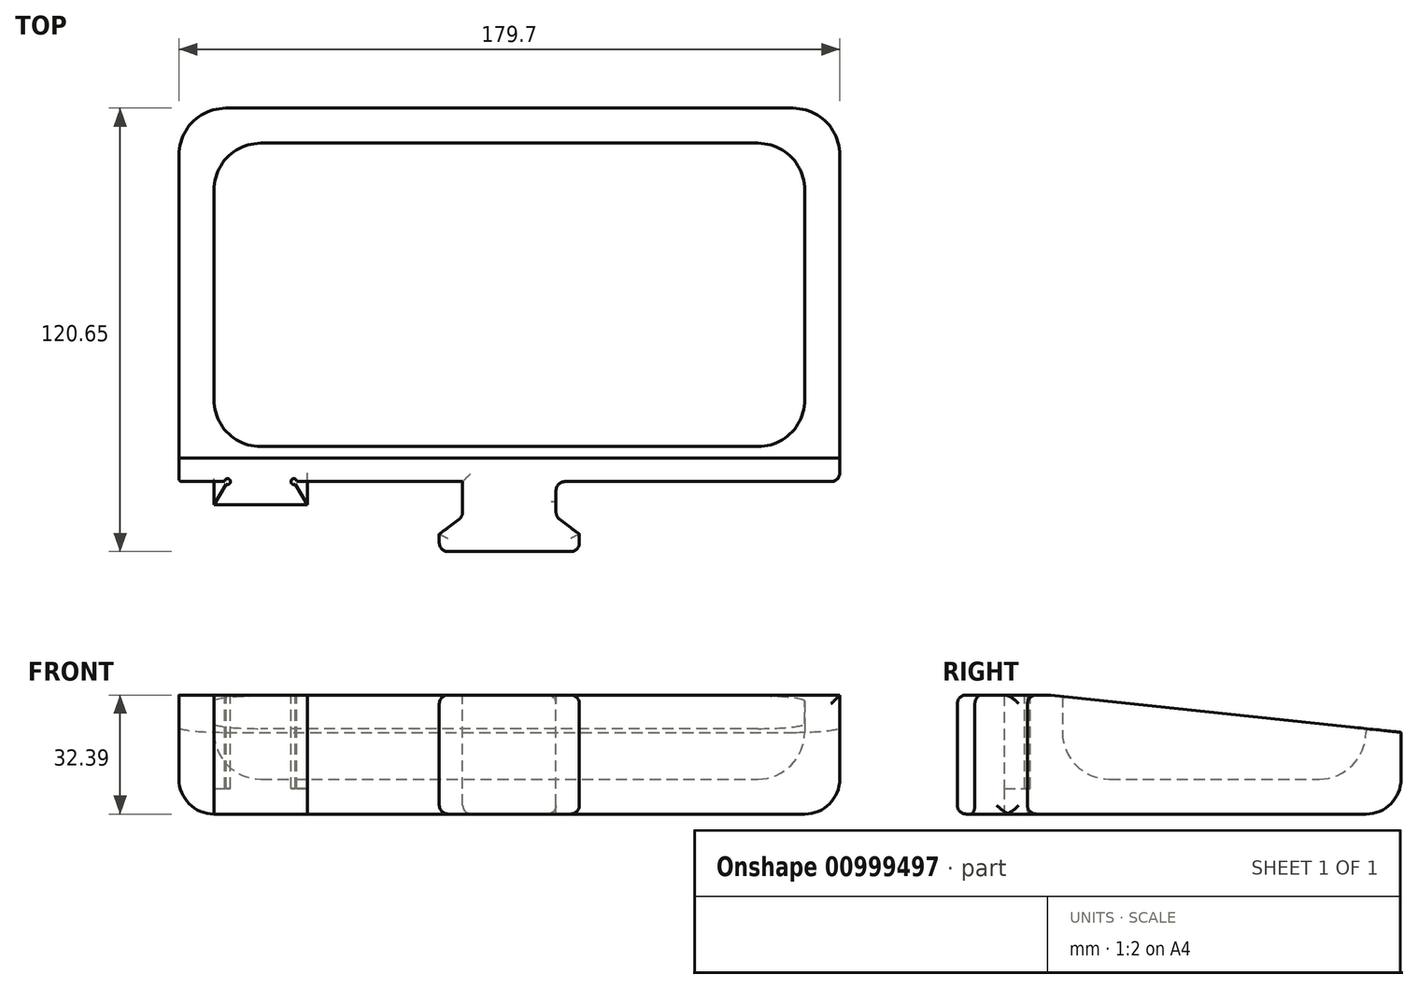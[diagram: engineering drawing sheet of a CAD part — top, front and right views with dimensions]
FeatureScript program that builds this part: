
annotation { "Feature Type Name" : "Feature", "Feature Type Description" : "" }
export const myFeature = defineFeature(function(context is Context, id is Id, definition is map)
    precondition{}
    {
        {
            var Q0;
            Q0=qCreatedBy(makeId("Top.planeOp"),FACE);
            var sketch = newSketch(context, id + "F0", { "sketchPlane" : qUnion([Q0])});
            skLineSegment(sketch, "E0.bottom", {"start": v(-89.85, -50.8) * mm, "end": v(89.85, -50.8) * mm});
            skLineSegment(sketch, "E0.top", {"start": v(-89.85, 50.8) * mm, "end": v(89.85, 50.8) * mm});
            skLineSegment(sketch, "E0.left", {"start": v(-89.85, -50.8) * mm, "end": v(-89.85, 50.8) * mm});
            skLineSegment(sketch, "E0.right", {"start": v(89.85, -50.8) * mm, "end": v(89.85, 50.8) * mm});
            skPoint(sketch, "E0.middle", {"position": v(0, 0) * mm});
            skSolve(sketch);
        }
        {
            var Q0;
            Q0=makeQuery(id+"F0.imprint","IMPRINT",FACE,{"disambiguationData":[TD([[makeQuery(id+"F0.imprint","IMPRINT",EDGE,{"derivedFrom":sQuery(id+"F0.wireOp",EDGE,"E0.bottom")}),1.0]])]});
            extrude(context, id + "F1", {"entities" : qUnion([Q0]), "depth" : 32.38 * mm, "offsetDistance" : 25.4 * mm});
        }
        {
            var Q0;
            Q0=makeQuery(id+"F1.opExtrude","SWEPT_FACE",FACE,{"disambiguationData":[OSD([sQuery(id+"F0.wireOp",EDGE,"E0.right")])]});
            var sketch = newSketch(context, id + "F2", { "sketchPlane" : qUnion([Q0])});
            skLineSegment(sketch, "E1", {"start": v(-44.45, 32.39) * mm, "end": v(50.8, 22.23) * mm});
            skLineSegment(sketch, "E2", {"start": v(50.8, 22.23) * mm, "end": v(50.8, 32.39) * mm});
            skLineSegment(sketch, "E3", {"start": v(50.8, 32.39) * mm, "end": v(-44.45, 32.39) * mm});
            skSolve(sketch);
        }
        {
            var Q0;
            Q0=makeQuery(id+"F4zIDM2y6RTGsAz_1.boolean.opBoolean","MERGE",FACE,{"derivedFrom":[makeQuery(id+"F1.opExtrude","CAP_FACE",FACE,{"disambiguationData":[OSD([sQuery(id+"F0.wireOp",EDGE,"E0.bottom"),sQuery(id+"F0.wireOp",EDGE,"E0.top"),sQuery(id+"F0.wireOp",EDGE,"E0.left"),sQuery(id+"F0.wireOp",EDGE,"E0.right")])],"isStart":false})],"fromTools":[makeQuery(id+"F4zIDM2y6RTGsAz_1.opExtrude","SWEPT_FACE",FACE,{"disambiguationData":[OSD([sQuery(id+"FbF38NB3fGvbLQ3_1.wireOp",EDGE,"ddc0e0ec-bf3b-4cb0-ae8b-31f4564a783b.bottom")])]})]});
            shell(context, id + "F3", {"entities" : qUnion([Q0]), "thickness" : 9.52 * mm});
        }
        {
            var Q0;
            Q0=makeQuery(id+"F2.imprint","IMPRINT",FACE,{"disambiguationData":[TD([[makeQuery(id+"F2.imprint","IMPRINT",EDGE,{"derivedFrom":sQuery(id+"F2.wireOp",EDGE,"E1")}),1.0]])]});
            extrude(context, id + "F4", {"entities" : qUnion([Q0]), "operationType" : NewBodyOperationType.REMOVE, "endBound" : BoundingType.THROUGH_ALL, "oppositeDirection" : true, "depth" : 25.4 * mm, "offsetDistance" : 25.4 * mm});
        }
        {
            var Q0;
            Q0=makeQuery(id+"Ffoehrqari5NT87_1.boolean.opBoolean","MERGE",FACE,{"derivedFrom":[makeQuery(id+"F1.opExtrude","SWEPT_FACE",FACE,{"disambiguationData":[OSD([sQuery(id+"F0.wireOp",EDGE,"E0.bottom")])]}),makeQuery(id+"Ffoehrqari5NT87_1.opExtrude","SWEPT_FACE",FACE,{"disambiguationData":[OSD([sQuery(id+"F7CfLhOei2jAQx5_1.wireOp",EDGE,"9709d949-b5b5-4919-9016-7ddb15cc25a9.left")])]})]});
            var sketch = newSketch(context, id + "F5", { "sketchPlane" : qUnion([Q0])});
            skLineSegment(sketch, "E4", {"start": v(0, 0) * mm, "end": v(0, 32.39) * mm, "construction": true});
            skLineSegment(sketch, "E5", {"start": v(-19.05, 0) * mm, "end": v(-19.05, 32.39) * mm});
            skLineSegment(sketch, "E6.MirrorCS", {"start": v(19.05, 0) * mm, "end": v(19.05, 32.39) * mm});
            skLineSegment(sketch, "E7", {"start": v(-19.05, 32.39) * mm, "end": v(19.05, 32.39) * mm});
            skLineSegment(sketch, "E8", {"start": v(-19.05, 0) * mm, "end": v(19.05, 0) * mm});
            skSolve(sketch);
        }
        {
            var Q0;
            Q0=makeQuery(id+"F5.imprint","IMPRINT",FACE,{"disambiguationData":[TD([[makeQuery(id+"F5.imprint","IMPRINT",EDGE,{"derivedFrom":sQuery(id+"F5.wireOp",EDGE,"E5")}),-1.0]])]});
            extrude(context, id + "F6", {"entities" : qUnion([Q0]), "operationType" : NewBodyOperationType.ADD, "depth" : 19.05 * mm, "offsetDistance" : 25.4 * mm});
        }
        {
            var Q0;
            {var subQ0=sQuery(id+"F0.wireOp",EDGE,"E0.left");var subQ1=makeQuery(id+"F1.opExtrude","SWEPT_FACE",FACE,{"disambiguationData":[OSD([subQ0])]});var subQ4=sQuery(id+"F0.wireOp",EDGE,"E0.bottom");Q0=makeQuery(id+"F6.boolean.opBoolean","SPLIT",FACE,{"disambiguationData":[TD([subQ1])],"derivedFrom":makeQuery(id+"F1.opExtrude","SWEPT_FACE",FACE,{"disambiguationData":[OSD([subQ4])]})});}
            var sketch = newSketch(context, id + "F7", { "sketchPlane" : qUnion([Q0])});
            skLineSegment(sketch, "E9.bottom", {"start": v(-80.33, 32.38) * mm, "end": v(-54.93, 32.39) * mm});
            skLineSegment(sketch, "E9.top", {"start": v(-80.33, 0) * mm, "end": v(-54.93, 0) * mm});
            skLineSegment(sketch, "E9.left", {"start": v(-80.33, 32.39) * mm, "end": v(-80.33, 0) * mm});
            skLineSegment(sketch, "E9.right", {"start": v(-54.93, 32.38) * mm, "end": v(-54.93, 0) * mm});
            skSolve(sketch);
        }
        {
            var Q0;
            Q0=makeQuery(id+"F7.imprint","IMPRINT",FACE,{"disambiguationData":[TD([[makeQuery(id+"F7.imprint","IMPRINT",EDGE,{"derivedFrom":sQuery(id+"F7.wireOp",EDGE,"E9.bottom")}),-1.0]])]});
            extrude(context, id + "F8", {"entities" : qUnion([Q0]), "operationType" : NewBodyOperationType.ADD, "depth" : 6.35 * mm, "offsetDistance" : 25.4 * mm});
        }
        {
            var Q0;
            Q0=makeQuery(id+"F8.boolean.opBoolean","MERGE",FACE,{"derivedFrom":[makeQuery(id+"F6.boolean.opBoolean","MERGE",FACE,{"derivedFrom":[makeQuery(id+"F1.opExtrude","CAP_FACE",FACE,{"disambiguationData":[OSD([sQuery(id+"F0.wireOp",EDGE,"E0.bottom"),sQuery(id+"F0.wireOp",EDGE,"E0.top"),sQuery(id+"F0.wireOp",EDGE,"E0.left"),sQuery(id+"F0.wireOp",EDGE,"E0.right")])],"isStart":false}),makeQuery(id+"F6.opExtrude","SWEPT_FACE",FACE,{"disambiguationData":[OSD([sQuery(id+"F5.wireOp",EDGE,"E7")])]})]}),makeQuery(id+"F8.opExtrude","SWEPT_FACE",FACE,{"disambiguationData":[OSD([sQuery(id+"F7.wireOp",EDGE,"E9.bottom")])]})]});
            var sketch = newSketch(context, id + "F9", { "sketchPlane" : qUnion([Q0])});
            skLineSegment(sketch, "E10", {"start": v(-80.33, -50.8) * mm, "end": v(-54.93, -50.8) * mm});
            skLineSegment(sketch, "E11", {"start": v(-80.33, -57.15) * mm, "end": v(-76.66, -50.8) * mm});
            skLineSegment(sketch, "E12", {"start": v(-67.63, -57.15) * mm, "end": v(-67.63, -50.8) * mm, "construction": true});
            skLineSegment(sketch, "E13.MirrorCS", {"start": v(-54.93, -57.15) * mm, "end": v(-58.6, -50.8) * mm});
            skCircle(sketch, "E14", {"center": v(-76.66, -50.8) * mm, "radius": 0.8 * mm});
            skCircle(sketch, "E15.MirrorC", {"center": v(-58.6, -50.8) * mm, "radius": 0.8 * mm});
            skSolve(sketch);
        }
        {
            var Q0;
            {var subQ11=sQuery(id+"F9.wireOp",EDGE,"E11");Q0=makeQuery(id+"F9.imprint","IMPRINT",FACE,{"disambiguationData":[TD([[makeQuery(id+"F9.imprint","IMPRINT",EDGE,{"derivedFrom":subQ11}),1.0]])]});}
            var Q1;
            {var subQ11=sQuery(id+"F9.wireOp",EDGE,"E13.MirrorCS");Q1=makeQuery(id+"F9.imprint","IMPRINT",FACE,{"disambiguationData":[TD([[makeQuery(id+"F9.imprint","IMPRINT",EDGE,{"derivedFrom":subQ11}),-1.0]])]});}
            var Q2;
            {var subQ3=sQuery(id+"F7.wireOp",EDGE,"E9.bottom");var subQ5=sQuery(id+"F0.wireOp",EDGE,"E0.bottom");var subQ8=sQuery(id+"F7.wireOp",EDGE,"E9.left");var subQ9=makeQuery(id+"F8.opExtrude","SWEPT_EDGE",EDGE,{"disambiguationData":[OSD([subQ5,subQ3,subQ8])]});Q2=makeQuery(id+"F9.imprint","IMPRINT",FACE,{"disambiguationData":[TD([[makeQuery(id+"F9.imprint","IMPRINT",EDGE,{"derivedFrom":subQ9}),-1.0]])]});}
            var Q3;
            {var subQ0=sQuery(id+"F9.wireOp",EDGE,"E14");var subQ1=sQuery(id+"F9.wireOp",EDGE,"E10");var subQ2=makeQuery(id+"F9.imprint","INTERSECT",VERTEX,{"disambiguationData":[OD(0.0)],"derivedFrom":[subQ1,subQ0]});Q3=makeQuery(id+"F9.imprint","IMPRINT",FACE,{"disambiguationData":[TD([[makeQuery(id+"F9.imprint","IMPRINT",EDGE,{"disambiguationData":[TD([[subQ2,1.0]])],"derivedFrom":subQ1}),-1.0]])]});}
            var Q4;
            {var subQ0=sQuery(id+"F9.wireOp",EDGE,"E14");var subQ1=sQuery(id+"F9.wireOp",EDGE,"E10");var subQ2=makeQuery(id+"F9.imprint","INTERSECT",VERTEX,{"disambiguationData":[OD(0.0)],"derivedFrom":[subQ1,subQ0]});Q4=makeQuery(id+"F9.imprint","IMPRINT",FACE,{"disambiguationData":[TD([[makeQuery(id+"F9.imprint","IMPRINT",EDGE,{"disambiguationData":[TD([[subQ2,1.0]])],"derivedFrom":subQ1}),1.0]])]});}
            var Q5;
            {var subQ4=sQuery(id+"F0.wireOp",EDGE,"E0.bottom");var subQ7=sQuery(id+"F7.wireOp",EDGE,"E9.bottom");var subQ8=sQuery(id+"F7.wireOp",EDGE,"E9.right");var subQ9=makeQuery(id+"F8.opExtrude","SWEPT_EDGE",EDGE,{"disambiguationData":[OSD([subQ4,subQ7,subQ8])]});Q5=makeQuery(id+"F9.imprint","IMPRINT",FACE,{"disambiguationData":[TD([[makeQuery(id+"F9.imprint","IMPRINT",EDGE,{"derivedFrom":subQ9}),1.0]])]});}
            var Q6;
            {var subQ0=sQuery(id+"F9.wireOp",EDGE,"E10");var subQ1=makeQuery(id+"F9.imprint","INTERSECT",VERTEX,{"derivedFrom":[subQ0,sQuery(id+"F9.wireOp",EDGE,"E13.MirrorCS")]});Q6=makeQuery(id+"F9.imprint","IMPRINT",FACE,{"disambiguationData":[TD([[makeQuery(id+"F9.imprint","IMPRINT",EDGE,{"disambiguationData":[TD([[subQ1,-1.0]])],"derivedFrom":subQ0}),1.0]])]});}
            var Q7;
            {var subQ0=sQuery(id+"F9.wireOp",EDGE,"E13.MirrorCS");var subQ1=sQuery(id+"F9.wireOp",EDGE,"E10");var subQ2=makeQuery(id+"F9.imprint","INTERSECT",VERTEX,{"derivedFrom":[subQ1,subQ0]});Q7=makeQuery(id+"F9.imprint","IMPRINT",FACE,{"disambiguationData":[TD([[makeQuery(id+"F9.imprint","IMPRINT",EDGE,{"disambiguationData":[TD([[subQ2,1.0]])],"derivedFrom":subQ1}),-1.0]])]});}
            extrude(context, id + "F10", {"entities" : qUnion([Q0, Q1, Q2, Q3, Q4, Q5, Q6, Q7]), "operationType" : NewBodyOperationType.REMOVE, "oppositeDirection" : true, "depth" : 25.4 * mm, "offsetDistance" : 25.4 * mm});
        }
        {
            var Q0;
            Q0=makeQuery(id+"F3.opShell","OFFSET_EDGE",EDGE,{"disambiguationData":[OSD([sQuery(id+"F0.wireOp",EDGE,"E0.bottom"),sQuery(id+"F0.wireOp",EDGE,"E0.left")])]});
            var Q1;
            Q1=makeQuery(id+"F3.opShell","OFFSET_EDGE",EDGE,{"disambiguationData":[OSD([sQuery(id+"F0.wireOp",EDGE,"E0.bottom"),sQuery(id+"F0.wireOp",EDGE,"E0.right")])]});
            var Q2;
            Q2=makeQuery(id+"F3.opShell","OFFSET_EDGE",EDGE,{"disambiguationData":[OSD([sQuery(id+"F0.wireOp",EDGE,"E0.top"),sQuery(id+"F0.wireOp",EDGE,"E0.right")])]});
            var Q3;
            Q3=makeQuery(id+"F3.opShell","OFFSET_EDGE",EDGE,{"disambiguationData":[OSD([sQuery(id+"F0.wireOp",EDGE,"E0.top"),sQuery(id+"F0.wireOp",EDGE,"E0.left")])]});
            var Q4;
            {var subQ0=sQuery(id+"F0.wireOp",EDGE,"E0.left");Q4=makeQuery(id+"F3.opShell","OFFSET_EDGE",EDGE,{"disambiguationData":[OSD([subQ0]),TDD([makeQuery(id+"F1.opExtrude","CAP_EDGE",EDGE,{"disambiguationData":[OSD([subQ0])],"isStart":true})])]});}
            var Q5;
            {var subQ0=sQuery(id+"F0.wireOp",EDGE,"E0.top");Q5=makeQuery(id+"F3.opShell","OFFSET_EDGE",EDGE,{"disambiguationData":[OSD([subQ0]),TDD([makeQuery(id+"F1.opExtrude","CAP_EDGE",EDGE,{"disambiguationData":[OSD([subQ0])],"isStart":true})])]});}
            var Q6;
            {var subQ0=sQuery(id+"F0.wireOp",EDGE,"E0.right");Q6=makeQuery(id+"F3.opShell","OFFSET_EDGE",EDGE,{"disambiguationData":[OSD([subQ0]),TDD([makeQuery(id+"F1.opExtrude","CAP_EDGE",EDGE,{"disambiguationData":[OSD([subQ0])],"isStart":true})])]});}
            var Q7;
            {var subQ0=sQuery(id+"F0.wireOp",EDGE,"E0.bottom");Q7=makeQuery(id+"F3.opShell","OFFSET_EDGE",EDGE,{"disambiguationData":[OSD([subQ0]),TDD([makeQuery(id+"F1.opExtrude","CAP_EDGE",EDGE,{"disambiguationData":[OSD([subQ0])],"isStart":true})])]});}
            fillet(context, id + "F11", {"entities" : qUnion([Q0, Q1, Q2, Q3, Q4, Q5, Q6, Q7]), "tangentPropagation" : true, "radius" : 12.7 * mm, "defaultsChanged" : false, "vertexSettings" : [], "allowEdgeOverflow" : false});
        }
        {
            var Q0;
            Q0=makeQuery(id+"F8.boolean.opBoolean","MERGE",FACE,{"derivedFrom":[makeQuery(id+"F6.boolean.opBoolean","MERGE",FACE,{"derivedFrom":[makeQuery(id+"F1.opExtrude","CAP_FACE",FACE,{"disambiguationData":[OSD([sQuery(id+"F0.wireOp",EDGE,"E0.bottom"),sQuery(id+"F0.wireOp",EDGE,"E0.top"),sQuery(id+"F0.wireOp",EDGE,"E0.left"),sQuery(id+"F0.wireOp",EDGE,"E0.right")])],"isStart":false}),makeQuery(id+"F6.opExtrude","SWEPT_FACE",FACE,{"disambiguationData":[OSD([sQuery(id+"F5.wireOp",EDGE,"E7")])]})]}),makeQuery(id+"F8.opExtrude","SWEPT_FACE",FACE,{"disambiguationData":[OSD([sQuery(id+"F7.wireOp",EDGE,"E9.bottom")])]})]});
            var sketch = newSketch(context, id + "F12", { "sketchPlane" : qUnion([Q0])});
            skLineSegment(sketch, "E16", {"start": v(-19.05, -65.09) * mm, "end": v(-12.7, -60.33) * mm});
            skPoint(sketch, "E16.endSnap0", {"position": v(-19.05, -60.33) * mm});
            skLineSegment(sketch, "E17", {"start": v(-12.7, -60.33) * mm, "end": v(-12.7, -50.8) * mm});
            skLineSegment(sketch, "E18", {"start": v(-12.7, -50.8) * mm, "end": v(-19.05, -50.8) * mm});
            skLineSegment(sketch, "E19", {"start": v(-19.05, -50.8) * mm, "end": v(-19.05, -65.09) * mm});
            skLineSegment(sketch, "E20", {"start": v(0, -69.85) * mm, "end": v(0, -50.8) * mm, "construction": true});
            skLineSegment(sketch, "E21", {"start": v(-19.05, -50.8) * mm, "end": v(19.05, -50.8) * mm});
            skLineSegment(sketch, "E22.MirrorCS", {"start": v(12.7, -60.33) * mm, "end": v(12.7, -50.8) * mm});
            skLineSegment(sketch, "E23.MirrorCS", {"start": v(12.7, -50.8) * mm, "end": v(19.05, -50.8) * mm});
            skLineSegment(sketch, "E24.MirrorCS", {"start": v(19.05, -50.8) * mm, "end": v(19.05, -65.09) * mm});
            skLineSegment(sketch, "E25.MirrorCS", {"start": v(19.05, -65.09) * mm, "end": v(12.7, -60.33) * mm});
            skSolve(sketch);
        }
        {
            var Q0;
            Q0=makeQuery(id+"F12.imprint","IMPRINT",FACE,{"disambiguationData":[TD([[makeQuery(id+"F12.imprint","IMPRINT",EDGE,{"derivedFrom":sQuery(id+"F12.wireOp",EDGE,"E16")}),1.0]])]});
            var Q1;
            Q1=makeQuery(id+"F12.imprint","IMPRINT",FACE,{"disambiguationData":[TD([[makeQuery(id+"F12.imprint","IMPRINT",EDGE,{"derivedFrom":sQuery(id+"F12.wireOp",EDGE,"0d325317-356d-4031-95fb-7e1340f61ca70.MirrorCS")}),-1.0]])]});
            var Q2;
            {var subQ4=sQuery(id+"F12.wireOp",EDGE,"E22.MirrorCS");Q2=makeQuery(id+"F12.imprint","IMPRINT",FACE,{"disambiguationData":[TD([[makeQuery(id+"F12.imprint","IMPRINT",EDGE,{"derivedFrom":subQ4}),-1.0]])]});}
            extrude(context, id + "F13", {"entities" : qUnion([Q0, Q1, Q2]), "operationType" : NewBodyOperationType.REMOVE, "endBound" : BoundingType.THROUGH_ALL, "oppositeDirection" : true, "depth" : 25.4 * mm, "offsetDistance" : 25.4 * mm});
        }
        {
            var Q0;
            Q0=makeQuery(id+"F1.opExtrude","SWEPT_EDGE",EDGE,{"disambiguationData":[OSD([sQuery(id+"F0.wireOp",EDGE,"E0.top"),sQuery(id+"F0.wireOp",EDGE,"E0.left")])]});
            var Q1;
            Q1=makeQuery(id+"F1.opExtrude","SWEPT_EDGE",EDGE,{"disambiguationData":[OSD([sQuery(id+"F0.wireOp",EDGE,"E0.top"),sQuery(id+"F0.wireOp",EDGE,"E0.right")])]});
            fillet(context, id + "F14", {"entities" : qUnion([Q0, Q1]), "tangentPropagation" : true, "radius" : 12.7 * mm, "defaultsChanged" : false, "vertexSettings" : [], "allowEdgeOverflow" : false});
        }
        {
            var Q0;
            Q0=makeQuery(id+"F4.boolean.opBoolean","COPY",EDGE,{"derivedFrom":makeQuery(id+"F4.opExtrude","CAP_EDGE",EDGE,{"disambiguationData":[OSD([sQuery(id+"F2.wireOp",EDGE,"E1")])],"isStart":true})});
            var Q1;
            {var subQ0=sQuery(id+"F0.wireOp",EDGE,"E0.left");var subQ1=sQuery(id+"F0.wireOp",EDGE,"E0.top");Q1=makeQuery(id+"F14.opFillet","BLEND_EDGE",EDGE,{"blendedFrom":[makeQuery(id+"F1.opExtrude","SWEPT_EDGE",EDGE,{"disambiguationData":[OSD([subQ1,subQ0])]}),makeQuery(id+"F8.boolean.opBoolean","MERGE",FACE,{"derivedFrom":[makeQuery(id+"F6.boolean.opBoolean","MERGE",FACE,{"derivedFrom":[makeQuery(id+"F1.opExtrude","CAP_FACE",FACE,{"disambiguationData":[OSD([sQuery(id+"F0.wireOp",EDGE,"E0.bottom"),subQ1,subQ0,sQuery(id+"F0.wireOp",EDGE,"E0.right")])],"isStart":true}),makeQuery(id+"F6.opExtrude","SWEPT_FACE",FACE,{"disambiguationData":[OSD([sQuery(id+"F5.wireOp",EDGE,"E8")])]})]}),makeQuery(id+"F8.opExtrude","SWEPT_FACE",FACE,{"disambiguationData":[OSD([sQuery(id+"F7.wireOp",EDGE,"E9.top")])]})]})],"blendedInto":[makeQuery(id+"F8.boolean.opBoolean","MERGE",FACE,{"derivedFrom":[makeQuery(id+"F6.boolean.opBoolean","MERGE",FACE,{"derivedFrom":[makeQuery(id+"F1.opExtrude","CAP_FACE",FACE,{"disambiguationData":[OSD([sQuery(id+"F0.wireOp",EDGE,"E0.bottom"),subQ1,subQ0,sQuery(id+"F0.wireOp",EDGE,"E0.right")])],"isStart":true}),makeQuery(id+"F6.opExtrude","SWEPT_FACE",FACE,{"disambiguationData":[OSD([sQuery(id+"F5.wireOp",EDGE,"E8")])]})]}),makeQuery(id+"F8.opExtrude","SWEPT_FACE",FACE,{"disambiguationData":[OSD([sQuery(id+"F7.wireOp",EDGE,"E9.top")])]})]})]});}
            fillet(context, id + "F15", {"entities" : qUnion([Q0, Q1]), "tangentPropagation" : true, "radius" : 9.52 * mm, "defaultsChanged" : false, "vertexSettings" : [], "allowEdgeOverflow" : false});
        }
        {
            var Q0;
            {var subQ0=sQuery(id+"F0.wireOp",EDGE,"E0.right");var subQ3=sQuery(id+"F0.wireOp",EDGE,"E0.bottom");Q0=makeQuery(id+"F13.boolean.opBoolean","MERGE",FACE,{"derivedFrom":[makeQuery(id+"F6.boolean.opBoolean","SPLIT",FACE,{"disambiguationData":[TD([makeQuery(id+"F1.opExtrude","SWEPT_FACE",FACE,{"disambiguationData":[OSD([subQ0])]})])],"derivedFrom":makeQuery(id+"F1.opExtrude","SWEPT_FACE",FACE,{"disambiguationData":[OSD([subQ3])]})})],"fromTools":[makeQuery(id+"F13.opExtrude","SWEPT_FACE",FACE,{"disambiguationData":[OSD([sQuery(id+"F12.wireOp",EDGE,"E21")])]})]});}
            var Q1;
            Q1=makeQuery(id+"F6.opExtrude","SWEPT_EDGE",EDGE,{"disambiguationData":[OSD([sQuery(id+"F0.wireOp",EDGE,"E0.bottom"),sQuery(id+"F5.wireOp",EDGE,"E6.MirrorCS"),sQuery(id+"F5.wireOp",EDGE,"E7")])]});
            var Q2;
            Q2=makeQuery(id+"F13.boolean.opBoolean","COPY",EDGE,{"derivedFrom":makeQuery(id+"F13.opExtrude","CAP_EDGE",EDGE,{"disambiguationData":[OSD([sQuery(id+"F12.wireOp",EDGE,"E25.MirrorCS")])],"isStart":true})});
            var Q3;
            Q3=makeQuery(id+"F6.opExtrude","SWEPT_EDGE",EDGE,{"disambiguationData":[OSD([sQuery(id+"F0.wireOp",EDGE,"E0.bottom"),sQuery(id+"F5.wireOp",EDGE,"E6.MirrorCS"),sQuery(id+"F5.wireOp",EDGE,"E8")])]});
            var Q4;
            Q4=makeQuery(id+"F13.boolean.opBoolean","INTERSECT",EDGE,{"derivedFrom":[makeQuery(id+"F8.boolean.opBoolean","MERGE",FACE,{"derivedFrom":[makeQuery(id+"F6.boolean.opBoolean","MERGE",FACE,{"derivedFrom":[makeQuery(id+"F1.opExtrude","CAP_FACE",FACE,{"disambiguationData":[OSD([sQuery(id+"F0.wireOp",EDGE,"E0.bottom"),sQuery(id+"F0.wireOp",EDGE,"E0.top"),sQuery(id+"F0.wireOp",EDGE,"E0.left"),sQuery(id+"F0.wireOp",EDGE,"E0.right")])],"isStart":true}),makeQuery(id+"F6.opExtrude","SWEPT_FACE",FACE,{"disambiguationData":[OSD([sQuery(id+"F5.wireOp",EDGE,"E8")])]})]}),makeQuery(id+"F8.opExtrude","SWEPT_FACE",FACE,{"disambiguationData":[OSD([sQuery(id+"F7.wireOp",EDGE,"E9.top")])]})]}),makeQuery(id+"F13.opExtrude","SWEPT_FACE",FACE,{"disambiguationData":[OSD([sQuery(id+"F12.wireOp",EDGE,"E25.MirrorCS")])]})]});
            var Q5;
            Q5=makeQuery(id+"F13.boolean.opBoolean","COPY",EDGE,{"derivedFrom":makeQuery(id+"F13.opExtrude","SWEPT_EDGE",EDGE,{"disambiguationData":[OSD([sQuery(id+"F12.wireOp",EDGE,"E22.MirrorCS"),sQuery(id+"F12.wireOp",EDGE,"E25.MirrorCS")])]})});
            var Q6;
            Q6=makeQuery(id+"F13.boolean.opBoolean","COPY",EDGE,{"derivedFrom":makeQuery(id+"F13.opExtrude","SWEPT_EDGE",EDGE,{"disambiguationData":[OSD([sQuery(id+"F0.wireOp",EDGE,"E0.bottom"),sQuery(id+"F5.wireOp",EDGE,"E6.MirrorCS"),sQuery(id+"F5.wireOp",EDGE,"E7"),sQuery(id+"F12.wireOp",EDGE,"E24.MirrorCS"),sQuery(id+"F12.wireOp",EDGE,"E25.MirrorCS")])]})});
            var Q7;
            Q7=makeQuery(id+"F6.opExtrude","SWEPT_EDGE",EDGE,{"disambiguationData":[OSD([sQuery(id+"F0.wireOp",EDGE,"E0.bottom"),sQuery(id+"F5.wireOp",EDGE,"E5"),sQuery(id+"F5.wireOp",EDGE,"E7")])]});
            var Q8;
            Q8=makeQuery(id+"F13.boolean.opBoolean","INTERSECT",EDGE,{"derivedFrom":[makeQuery(id+"F8.boolean.opBoolean","MERGE",FACE,{"derivedFrom":[makeQuery(id+"F6.boolean.opBoolean","MERGE",FACE,{"derivedFrom":[makeQuery(id+"F1.opExtrude","CAP_FACE",FACE,{"disambiguationData":[OSD([sQuery(id+"F0.wireOp",EDGE,"E0.bottom"),sQuery(id+"F0.wireOp",EDGE,"E0.top"),sQuery(id+"F0.wireOp",EDGE,"E0.left"),sQuery(id+"F0.wireOp",EDGE,"E0.right")])],"isStart":true}),makeQuery(id+"F6.opExtrude","SWEPT_FACE",FACE,{"disambiguationData":[OSD([sQuery(id+"F5.wireOp",EDGE,"E8")])]})]}),makeQuery(id+"F8.opExtrude","SWEPT_FACE",FACE,{"disambiguationData":[OSD([sQuery(id+"F7.wireOp",EDGE,"E9.top")])]})]}),makeQuery(id+"F13.opExtrude","SWEPT_FACE",FACE,{"disambiguationData":[OSD([sQuery(id+"F12.wireOp",EDGE,"E17")])]})]});
            var Q9;
            Q9=makeQuery(id+"F6.opExtrude","SWEPT_EDGE",EDGE,{"disambiguationData":[OSD([sQuery(id+"F0.wireOp",EDGE,"E0.bottom"),sQuery(id+"F5.wireOp",EDGE,"E5"),sQuery(id+"F5.wireOp",EDGE,"E8")])]});
            var Q10;
            Q10=makeQuery(id+"F13.boolean.opBoolean","INTERSECT",EDGE,{"derivedFrom":[makeQuery(id+"F8.boolean.opBoolean","MERGE",FACE,{"derivedFrom":[makeQuery(id+"F6.boolean.opBoolean","MERGE",FACE,{"derivedFrom":[makeQuery(id+"F1.opExtrude","CAP_FACE",FACE,{"disambiguationData":[OSD([sQuery(id+"F0.wireOp",EDGE,"E0.bottom"),sQuery(id+"F0.wireOp",EDGE,"E0.top"),sQuery(id+"F0.wireOp",EDGE,"E0.left"),sQuery(id+"F0.wireOp",EDGE,"E0.right")])],"isStart":true}),makeQuery(id+"F6.opExtrude","SWEPT_FACE",FACE,{"disambiguationData":[OSD([sQuery(id+"F5.wireOp",EDGE,"E8")])]})]}),makeQuery(id+"F8.opExtrude","SWEPT_FACE",FACE,{"disambiguationData":[OSD([sQuery(id+"F7.wireOp",EDGE,"E9.top")])]})]}),makeQuery(id+"F13.opExtrude","SWEPT_FACE",FACE,{"disambiguationData":[OSD([sQuery(id+"F12.wireOp",EDGE,"E16")])]})]});
            var Q11;
            Q11=makeQuery(id+"F13.boolean.opBoolean","COPY",EDGE,{"derivedFrom":makeQuery(id+"F13.opExtrude","SWEPT_EDGE",EDGE,{"disambiguationData":[OSD([sQuery(id+"F12.wireOp",EDGE,"E16"),sQuery(id+"F12.wireOp",EDGE,"E17")])]})});
            var Q12;
            Q12=makeQuery(id+"F13.boolean.opBoolean","COPY",EDGE,{"derivedFrom":makeQuery(id+"F13.opExtrude","SWEPT_EDGE",EDGE,{"disambiguationData":[OSD([sQuery(id+"F0.wireOp",EDGE,"E0.bottom"),sQuery(id+"F5.wireOp",EDGE,"E5"),sQuery(id+"F5.wireOp",EDGE,"E7"),sQuery(id+"F12.wireOp",EDGE,"E16"),sQuery(id+"F12.wireOp",EDGE,"E19")])]})});
            var Q13;
            Q13=makeQuery(id+"F6.opExtrude","CAP_FACE",FACE,{"disambiguationData":[OSD([sQuery(id+"F5.wireOp",EDGE,"E5"),sQuery(id+"F5.wireOp",EDGE,"E6.MirrorCS"),sQuery(id+"F5.wireOp",EDGE,"E7"),sQuery(id+"F5.wireOp",EDGE,"E8")])],"isStart":false});
            var Q14;
            Q14=makeQuery(id+"F13.boolean.opBoolean","INTERSECT",EDGE,{"derivedFrom":[makeQuery(id+"F8.boolean.opBoolean","MERGE",FACE,{"derivedFrom":[makeQuery(id+"F6.boolean.opBoolean","MERGE",FACE,{"derivedFrom":[makeQuery(id+"F1.opExtrude","CAP_FACE",FACE,{"disambiguationData":[OSD([sQuery(id+"F0.wireOp",EDGE,"E0.bottom"),sQuery(id+"F0.wireOp",EDGE,"E0.top"),sQuery(id+"F0.wireOp",EDGE,"E0.left"),sQuery(id+"F0.wireOp",EDGE,"E0.right")])],"isStart":true}),makeQuery(id+"F6.opExtrude","SWEPT_FACE",FACE,{"disambiguationData":[OSD([sQuery(id+"F5.wireOp",EDGE,"E8")])]})]}),makeQuery(id+"F8.opExtrude","SWEPT_FACE",FACE,{"disambiguationData":[OSD([sQuery(id+"F7.wireOp",EDGE,"E9.top")])]})]}),makeQuery(id+"F13.opExtrude","SWEPT_FACE",FACE,{"disambiguationData":[OSD([sQuery(id+"F12.wireOp",EDGE,"E18")])]})]});
            var Q15;
            Q15=makeQuery(id+"F13.boolean.opBoolean","COPY",EDGE,{"derivedFrom":makeQuery(id+"F13.opExtrude","CAP_EDGE",EDGE,{"disambiguationData":[OSD([sQuery(id+"F12.wireOp",EDGE,"E17")])],"isStart":true})});
            fillet(context, id + "F16", {"entities" : qUnion([Q0, Q1, Q2, Q3, Q4, Q5, Q6, Q7, Q8, Q9, Q10, Q11, Q12, Q13, Q14, Q15]), "tangentPropagation" : true, "radius" : 2.38 * mm, "defaultsChanged" : false, "vertexSettings" : [], "allowEdgeOverflow" : false});
        }
        {
            var Q0;
            {var subQ0=sQuery(id+"F9.wireOp",EDGE,"E10");var subQ1=makeQuery(id+"F6.opExtrude","SWEPT_FACE",FACE,{"disambiguationData":[OSD([sQuery(id+"F5.wireOp",EDGE,"E5")])]});var subQ3=sQuery(id+"F0.wireOp",EDGE,"E0.left");var subQ4=sQuery(id+"F0.wireOp",EDGE,"E0.bottom");var subQ9=makeQuery(id+"F8.boolean.opBoolean","SPLIT",EDGE,{"disambiguationData":[TD([subQ1])],"derivedFrom":makeQuery(id+"F6.boolean.opBoolean","SPLIT",EDGE,{"disambiguationData":[TD([makeQuery(id+"F1.opExtrude","SWEPT_FACE",FACE,{"disambiguationData":[OSD([subQ3])]})])],"derivedFrom":makeQuery(id+"F1.opExtrude","CAP_EDGE",EDGE,{"disambiguationData":[OSD([subQ4])],"isStart":false})})});Q0=makeQuery(id+"F13.boolean.opBoolean","MERGE",EDGE,{"derivedFrom":[makeQuery(id+"F10.boolean.opBoolean","MERGE",EDGE,{"derivedFrom":[subQ9],"fromTools":[makeQuery(id+"F10.opExtrude","CAP_EDGE",EDGE,{"disambiguationData":[OSD([subQ0]),TDD([makeQuery(id+"F9.imprint","IMPRINT",EDGE,{"disambiguationData":[TD([[makeQuery(id+"F9.imprint","INTERSECT",VERTEX,{"disambiguationData":[OD(1.0)],"derivedFrom":[subQ0,sQuery(id+"F9.wireOp",EDGE,"E15.MirrorC")]}),-1.0]])],"derivedFrom":subQ0})])],"isStart":true})]})],"fromTools":[makeQuery(id+"F13.opExtrude","CAP_EDGE",EDGE,{"disambiguationData":[OSD([sQuery(id+"F12.wireOp",EDGE,"E18")])],"isStart":true})]});}
            var Q1;
            Q1=makeQuery(id+"F1.opExtrude","SWEPT_EDGE",EDGE,{"disambiguationData":[OSD([sQuery(id+"F0.wireOp",EDGE,"E0.bottom"),sQuery(id+"F0.wireOp",EDGE,"E0.left")])]});
            var Q2;
            {var subQ0=sQuery(id+"F9.wireOp",EDGE,"E10");var subQ1=sQuery(id+"F0.wireOp",EDGE,"E0.left");var subQ2=makeQuery(id+"F1.opExtrude","SWEPT_FACE",FACE,{"disambiguationData":[OSD([subQ1])]});var subQ5=sQuery(id+"F0.wireOp",EDGE,"E0.bottom");var subQ9=makeQuery(id+"F8.boolean.opBoolean","SPLIT",EDGE,{"disambiguationData":[TD([subQ2])],"derivedFrom":makeQuery(id+"F6.boolean.opBoolean","SPLIT",EDGE,{"disambiguationData":[TD([subQ2])],"derivedFrom":makeQuery(id+"F1.opExtrude","CAP_EDGE",EDGE,{"disambiguationData":[OSD([subQ5])],"isStart":false})})});Q2=makeQuery(id+"F10.boolean.opBoolean","MERGE",EDGE,{"derivedFrom":[subQ9],"fromTools":[makeQuery(id+"F10.opExtrude","CAP_EDGE",EDGE,{"disambiguationData":[OSD([subQ0]),TDD([makeQuery(id+"F9.imprint","IMPRINT",EDGE,{"disambiguationData":[TD([[makeQuery(id+"F9.imprint","INTERSECT",VERTEX,{"disambiguationData":[OD(1.0)],"derivedFrom":[subQ0,sQuery(id+"F9.wireOp",EDGE,"E14")]}),1.0]])],"derivedFrom":subQ0})])],"isStart":true})]});}
            var Q3;
            {var subQ0=sQuery(id+"F9.wireOp",EDGE,"E10");var subQ1=sQuery(id+"F0.wireOp",EDGE,"E0.left");var subQ2=makeQuery(id+"F1.opExtrude","SWEPT_FACE",FACE,{"disambiguationData":[OSD([subQ1])]});var subQ8=sQuery(id+"F0.wireOp",EDGE,"E0.bottom");var subQ10=makeQuery(id+"F1.opExtrude","SWEPT_FACE",FACE,{"disambiguationData":[OSD([subQ8])]});Q3=makeQuery(id+"F15.opFillet","BLEND_EDGE",EDGE,{"blendedFrom":[makeQuery(id+"F4.boolean.opBoolean","INTERSECT",EDGE,{"derivedFrom":[subQ2,makeQuery(id+"F4.opExtrude","SWEPT_FACE",FACE,{"disambiguationData":[OSD([sQuery(id+"F2.wireOp",EDGE,"E1")])]})]}),makeQuery(id+"F10.boolean.opBoolean","MERGE",FACE,{"derivedFrom":[makeQuery(id+"F8.boolean.opBoolean","SPLIT",FACE,{"disambiguationData":[TD([subQ2])],"derivedFrom":makeQuery(id+"F6.boolean.opBoolean","SPLIT",FACE,{"disambiguationData":[TD([subQ2])],"derivedFrom":subQ10})})],"fromTools":[makeQuery(id+"F10.opExtrude","SWEPT_FACE",FACE,{"disambiguationData":[OSD([subQ0]),TDD([makeQuery(id+"F9.imprint","IMPRINT",EDGE,{"disambiguationData":[TD([[makeQuery(id+"F9.imprint","INTERSECT",VERTEX,{"disambiguationData":[OD(1.0)],"derivedFrom":[subQ0,sQuery(id+"F9.wireOp",EDGE,"E14")]}),1.0]])],"derivedFrom":subQ0})])]})]})],"blendedInto":[makeQuery(id+"F10.boolean.opBoolean","MERGE",FACE,{"derivedFrom":[makeQuery(id+"F8.boolean.opBoolean","SPLIT",FACE,{"disambiguationData":[TD([subQ2])],"derivedFrom":makeQuery(id+"F6.boolean.opBoolean","SPLIT",FACE,{"disambiguationData":[TD([subQ2])],"derivedFrom":subQ10})})],"fromTools":[makeQuery(id+"F10.opExtrude","SWEPT_FACE",FACE,{"disambiguationData":[OSD([subQ0]),TDD([makeQuery(id+"F9.imprint","IMPRINT",EDGE,{"disambiguationData":[TD([[makeQuery(id+"F9.imprint","INTERSECT",VERTEX,{"disambiguationData":[OD(1.0)],"derivedFrom":[subQ0,sQuery(id+"F9.wireOp",EDGE,"E14")]}),1.0]])],"derivedFrom":subQ0})])]})]})]});}
            var Q4;
            {var subQ0=sQuery(id+"F9.wireOp",EDGE,"E10");var subQ1=sQuery(id+"F0.wireOp",EDGE,"E0.left");var subQ2=makeQuery(id+"F1.opExtrude","SWEPT_FACE",FACE,{"disambiguationData":[OSD([subQ1])]});var subQ8=sQuery(id+"F0.wireOp",EDGE,"E0.bottom");var subQ10=makeQuery(id+"F1.opExtrude","SWEPT_FACE",FACE,{"disambiguationData":[OSD([subQ8])]});Q4=makeQuery(id+"F15.opFillet","BLEND_EDGE",EDGE,{"blendedFrom":[makeQuery(id+"F1.opExtrude","CAP_EDGE",EDGE,{"disambiguationData":[OSD([subQ1])],"isStart":true}),makeQuery(id+"F10.boolean.opBoolean","MERGE",FACE,{"derivedFrom":[makeQuery(id+"F8.boolean.opBoolean","SPLIT",FACE,{"disambiguationData":[TD([subQ2])],"derivedFrom":makeQuery(id+"F6.boolean.opBoolean","SPLIT",FACE,{"disambiguationData":[TD([subQ2])],"derivedFrom":subQ10})})],"fromTools":[makeQuery(id+"F10.opExtrude","SWEPT_FACE",FACE,{"disambiguationData":[OSD([subQ0]),TDD([makeQuery(id+"F9.imprint","IMPRINT",EDGE,{"disambiguationData":[TD([[makeQuery(id+"F9.imprint","INTERSECT",VERTEX,{"disambiguationData":[OD(1.0)],"derivedFrom":[subQ0,sQuery(id+"F9.wireOp",EDGE,"E14")]}),1.0]])],"derivedFrom":subQ0})])]})]})],"blendedInto":[makeQuery(id+"F10.boolean.opBoolean","MERGE",FACE,{"derivedFrom":[makeQuery(id+"F8.boolean.opBoolean","SPLIT",FACE,{"disambiguationData":[TD([subQ2])],"derivedFrom":makeQuery(id+"F6.boolean.opBoolean","SPLIT",FACE,{"disambiguationData":[TD([subQ2])],"derivedFrom":subQ10})})],"fromTools":[makeQuery(id+"F10.opExtrude","SWEPT_FACE",FACE,{"disambiguationData":[OSD([subQ0]),TDD([makeQuery(id+"F9.imprint","IMPRINT",EDGE,{"disambiguationData":[TD([[makeQuery(id+"F9.imprint","INTERSECT",VERTEX,{"disambiguationData":[OD(1.0)],"derivedFrom":[subQ0,sQuery(id+"F9.wireOp",EDGE,"E14")]}),1.0]])],"derivedFrom":subQ0})])]})]})]});}
            fillet(context, id + "F17", {"entities" : qUnion([Q0, Q1, Q2, Q3, Q4]), "radius" : 0.8 * mm, "defaultsChanged" : false, "vertexSettings" : [], "allowEdgeOverflow" : false});
        }
    });
